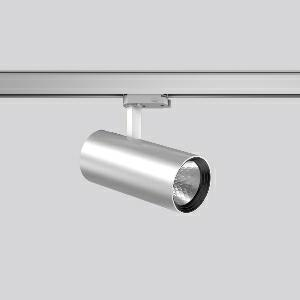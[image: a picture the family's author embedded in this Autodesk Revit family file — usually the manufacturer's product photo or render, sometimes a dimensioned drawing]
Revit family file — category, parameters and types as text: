
# Revit family: deecos_s_mini_742197_004_3_d995
name_source: partatom
category: Lighting Fixtures
units: mm (PartAtom-declared; Revit-internal decimal feet)

## family parameters
Cut with Voids When Loaded = No
Host = Face
Light Source = No
Part Type = Normal
Room Calculation Point = No
Round Connector Dimension = Use Diameter
Shared = No

## types (1)
- DEECOS S mini (1 x LED Modul 935, 2650 lm, 3500)
    Apparent Load = 20 VA
    Approval mark = CE
    CIE Flux Codes = 95 99 100 100 100
    Color Rendering = 92
    Color Temperature = 3500
    Default Elevation = 1800 mm
    Description = Series: DEECOS S mini
LED surface-mounted projector in modern design with no visible cooling ribs. Housing: die-cast aluminium, powder-coated. Rotation range: 356°. Swivel range: 90°. Black plastic ring and recessed LED to prevent glare from the side. Optical assembly with reflector made of MIRO-Silver with 98% total light reflection for outstanding efficiency - can be changed without tools. Best colour rendering index Ra>90. With multi adaptor for 3-circuit tracks 230 V. Suitable for Track on ceiling, Wall track. High quality converter without flickering and stroboscopic effect. The following accessories can be mounted without use of tools: interchangeable lenses, decorative glasses, honeycomb louvre, clear and frosted diffusers, white interchangeable plastic ring. 
Colour: silver
Diameter: 87 mm
Height: 214 mm
Lamp: LED
Socket: without socket
Colour temperature: 3500K
Colour rendering index (CRI): 92
System power: 20 W
Rated luminous flux: 2650 lm
Luminous efficiency: 133 lm/W
Control gear: Regulated power supply
Protection class: I
Type of protection: IP 20
    Height = 214 mm
    Lamp = 1 x LED Modul 935
    Lamp Light Flux = 2650 lm
    Lamp count = 1
    Length = 87 mm
    Lifetime = 50000 h
    Luminous efficacy = 133 lm/W
    Manufacturer = RZB
    ModVariant = No
    Model = 742197.004.3
    Mounting Place = Ceiling
    Mounting Type = Rail mounted
    Number of Poles = 1
    OnlyDefault = Yes
    Power Factor = 1
    Product Name = DEECOS S mini
    Product group = Track mounted projectors
    ProductGroupID = 301
    Protection Class = Protection class I
    Protection Degree = IP 20
    RLX_Detail_Level = 1
    RLX_Emergency_Light_Flux = 0 lm
    RLX_Emergency_Type = 0
    RLX_Emergency_Type_DB = No
    RlxData = <blob elided: 37505 chars, md5=87263dec>
    Socket = socket
    Standby Power = 0 W
    System Light Flux = 2650 lm
    System Power = 20 W
    Type Comments = Product without accessories
    Type Image = 741926.004.jpg
    URL = http://relux.com
    VarID = ---
    Voltage = 230 V
    Voltage Range = 220-240 V
    Weight = 0.00 kg
    Width = 0 mm  [stored 0 ft]

note: [stored X ft] marks values corroborated as IEEE doubles in the binary element streams (Revit-internal decimal feet)

## geometry (parser evidence)
native form markers: Blend x4, Sweep x13
no freeform markers — native parametric forms only
